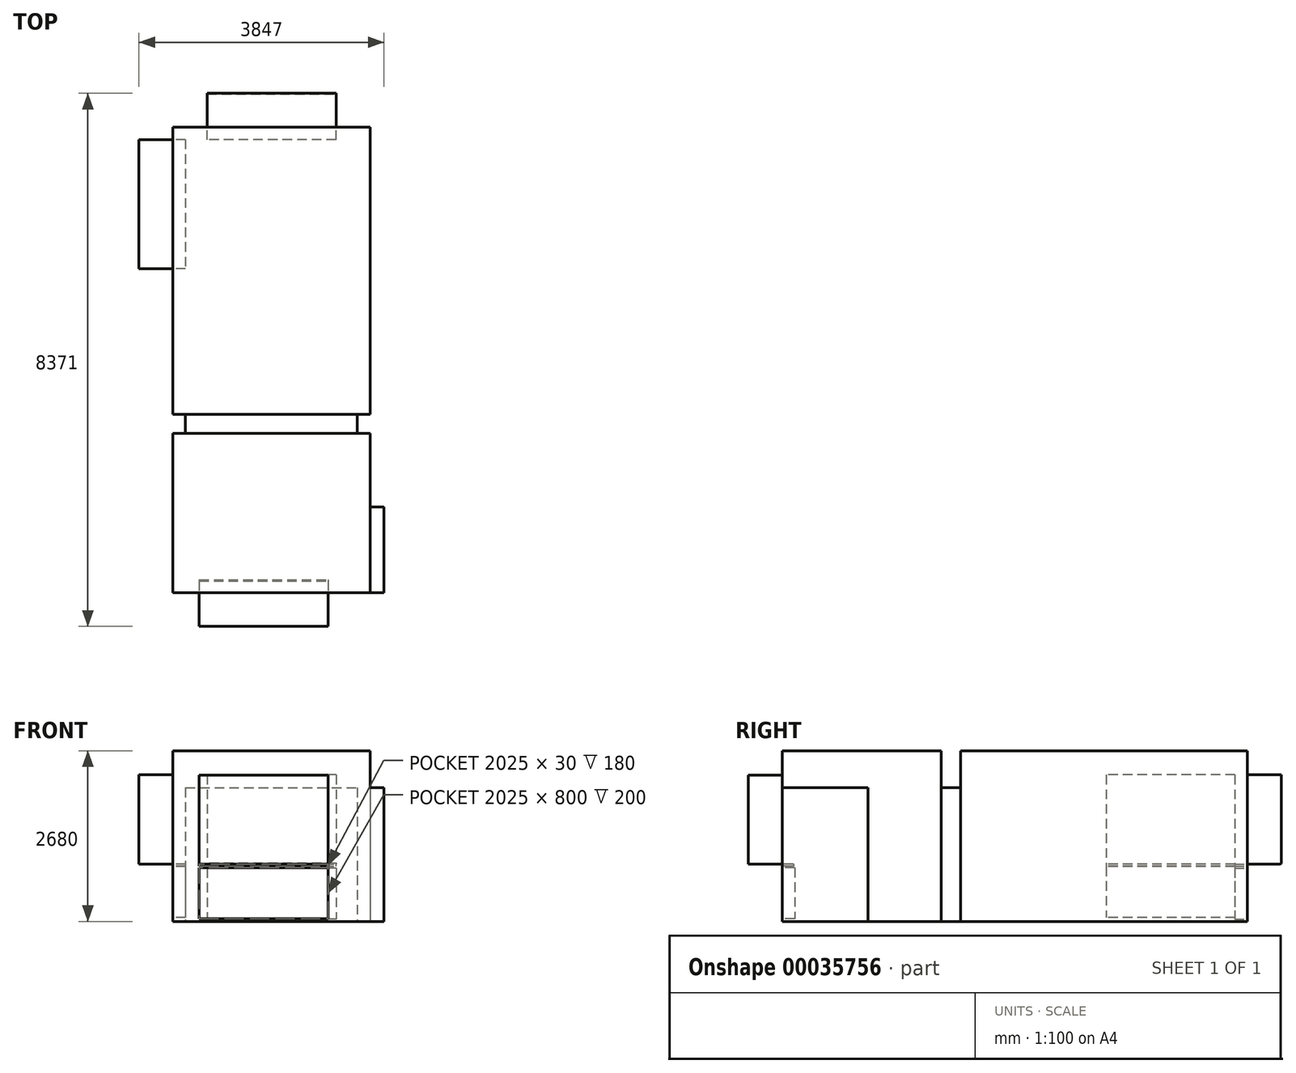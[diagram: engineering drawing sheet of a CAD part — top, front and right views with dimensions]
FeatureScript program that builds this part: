
annotation { "Feature Type Name" : "Feature", "Feature Type Description" : "" }
export const myFeature = defineFeature(function(context is Context, id is Id, definition is map)
    precondition{}
    {
        {
            var Q0;
            Q0=qCreatedBy(makeId("Top.planeOp"),FACE);
            var sketch = newSketch(context, id + "F0", { "sketchPlane" : qUnion([Q0])});
            skLineSegment(sketch, "E0.bottom", {"start": v(-1549.14, 3434.73) * mm, "end": v(1546.86, 3434.73) * mm});
            skLineSegment(sketch, "E0.top", {"start": v(-1549.14, -1072.27) * mm, "end": v(1546.86, -1072.27) * mm});
            skLineSegment(sketch, "E0.left", {"start": v(-1549.14, 3434.73) * mm, "end": v(-1549.14, -1072.27) * mm});
            skLineSegment(sketch, "E0.right", {"start": v(1546.86, 3434.73) * mm, "end": v(1546.86, -1072.27) * mm});
            skSolve(sketch);
        }
        {
            var Q0;
            Q0=makeQuery(id+"F0.imprint","IMPRINT",FACE,{"disambiguationData":[TD([[makeQuery(id+"F0.imprint","IMPRINT",EDGE,{"derivedFrom":sQuery(id+"F0.wireOp",EDGE,"E0.bottom")}),-1.0]])]});
            extrude(context, id + "F1", {"entities" : qUnion([Q0]), "depth" : 2680 * mm});
        }
        {
            var Q0;
            Q0=makeQuery(id+"F1.opExtrude","SWEPT_FACE",FACE,{"disambiguationData":[OSD([sQuery(id+"F0.wireOp",EDGE,"E0.bottom")])]});
            var sketch = newSketch(context, id + "F2", { "sketchPlane" : qUnion([Q0])});
            skLineSegment(sketch, "E1.bottom", {"start": v(-1013.86, 2300) * mm, "end": v(1011.14, 2300) * mm});
            skLineSegment(sketch, "E1.top", {"start": v(-1013.86, 900) * mm, "end": v(1011.14, 900) * mm});
            skLineSegment(sketch, "E1.left", {"start": v(-1013.86, 2300) * mm, "end": v(-1013.86, 900) * mm});
            skLineSegment(sketch, "E1.right", {"start": v(1011.14, 2300) * mm, "end": v(1011.14, 900) * mm});
            skSolve(sketch);
        }
        {
            var Q0;
            Q0=qSketchRegion(id+"F2",true);
            extrude(context, id + "F3", {"entities" : qUnion([Q0]), "operationType" : NewBodyOperationType.ADD, "depth" : 532 * mm});
        }
        {
            var Q0;
            Q0=makeQuery(id+"F1.opExtrude","SWEPT_FACE",FACE,{"disambiguationData":[OSD([sQuery(id+"F0.wireOp",EDGE,"E0.left")])]});
            var sketch = newSketch(context, id + "F4", { "sketchPlane" : qUnion([Q0])});
            skLineSegment(sketch, "E2.bottom", {"start": v(-3238.73, 2300) * mm, "end": v(-1213.73, 2300) * mm});
            skLineSegment(sketch, "E2.top", {"start": v(-3238.73, 900) * mm, "end": v(-1213.73, 900) * mm});
            skLineSegment(sketch, "E2.left", {"start": v(-3238.73, 2300) * mm, "end": v(-3238.73, 900) * mm});
            skLineSegment(sketch, "E2.right", {"start": v(-1213.73, 2300) * mm, "end": v(-1213.73, 900) * mm});
            skSolve(sketch);
        }
        {
            var Q0;
            Q0=makeQuery(id+"F4.imprint","IMPRINT",FACE,{"disambiguationData":[TD([[makeQuery(id+"F4.imprint","IMPRINT",EDGE,{"derivedFrom":sQuery(id+"F4.wireOp",EDGE,"E2.bottom")}),-1.0]])]});
            extrude(context, id + "F5", {"entities" : qUnion([Q0]), "operationType" : NewBodyOperationType.ADD, "depth" : 532 * mm});
        }
        {
            var Q0;
            Q0=makeQuery(id+"F1.opExtrude","SWEPT_FACE",FACE,{"disambiguationData":[OSD([sQuery(id+"F0.wireOp",EDGE,"E0.bottom")])]});
            var sketch = newSketch(context, id + "F6", { "sketchPlane" : qUnion([Q0])});
            skLineSegment(sketch, "E3", {"start": v(1011.14, 900) * mm, "end": v(-1013.86, 900) * mm});
            skLineSegment(sketch, "E4.left", {"start": v(-1013.86, 835) * mm, "end": v(-1013.86, 35) * mm});
            skLineSegment(sketch, "E5.bottom", {"start": v(-1013.86, 835) * mm, "end": v(1011.14, 835) * mm});
            skLineSegment(sketch, "E5.top", {"start": v(-1013.86, 35) * mm, "end": v(1011.14, 35) * mm});
            skLineSegment(sketch, "E5.right", {"start": v(1011.14, 835) * mm, "end": v(1011.14, 35) * mm});
            skSolve(sketch);
        }
        {
            var Q0;
            Q0=makeQuery(id+"F6.imprint","IMPRINT",FACE,{"disambiguationData":[TD([[makeQuery(id+"F6.imprint","IMPRINT",EDGE,{"derivedFrom":sQuery(id+"F6.wireOp",EDGE,"E5.bottom")}),-1.0]])]});
            extrude(context, id + "F7", {"entities" : qUnion([Q0]), "operationType" : NewBodyOperationType.REMOVE, "oppositeDirection" : true, "depth" : 200 * mm});
        }
        {
            var Q0;
            Q0=makeQuery(id+"F1.opExtrude","CAP_FACE",FACE,{"disambiguationData":[OSD([sQuery(id+"F0.wireOp",EDGE,"E0.bottom"),sQuery(id+"F0.wireOp",EDGE,"E0.top"),sQuery(id+"F0.wireOp",EDGE,"E0.left"),sQuery(id+"F0.wireOp",EDGE,"E0.right")])],"isStart":true});
            var sketch = newSketch(context, id + "F8", { "sketchPlane" : qUnion([Q0])});
            skLineSegment(sketch, "E6", {"start": v(-1351.14, 1072.27) * mm, "end": v(-1351.14, 1375.27) * mm});
            skLineSegment(sketch, "E7", {"start": v(-1351.14, 1375.27) * mm, "end": v(1348.86, 1375.27) * mm});
            skLineSegment(sketch, "E8", {"start": v(1348.86, 1375.27) * mm, "end": v(1348.86, 1072.27) * mm});
            skLineSegment(sketch, "E9", {"start": v(1348.86, 1072.27) * mm, "end": v(-1351.14, 1072.27) * mm});
            skSolve(sketch);
        }
        {
            var Q0;
            Q0=makeQuery(id+"F8.imprint","IMPRINT",FACE,{"disambiguationData":[TD([[makeQuery(id+"F8.imprint","IMPRINT",EDGE,{"derivedFrom":sQuery(id+"F8.wireOp",EDGE,"E6")}),-1.0]])]});
            extrude(context, id + "F9", {"entities" : qUnion([Q0]), "operationType" : NewBodyOperationType.ADD, "oppositeDirection" : true, "depth" : 2100 * mm});
        }
        {
            var Q0;
            Q0=makeQuery(id+"F9.boolean.opBoolean","MERGE",FACE,{"derivedFrom":[makeQuery(id+"F1.opExtrude","CAP_FACE",FACE,{"disambiguationData":[OSD([sQuery(id+"F0.wireOp",EDGE,"E0.bottom"),sQuery(id+"F0.wireOp",EDGE,"E0.top"),sQuery(id+"F0.wireOp",EDGE,"E0.left"),sQuery(id+"F0.wireOp",EDGE,"E0.right")])],"isStart":true}),makeQuery(id+"F9.opExtrude","CAP_FACE",FACE,{"disambiguationData":[OSD([sQuery(id+"F8.wireOp",EDGE,"E6"),sQuery(id+"F8.wireOp",EDGE,"E7"),sQuery(id+"F8.wireOp",EDGE,"E8"),sQuery(id+"F8.wireOp",EDGE,"E9")])],"isStart":true})]});
            var sketch = newSketch(context, id + "F10", { "sketchPlane" : qUnion([Q0])});
            skLineSegment(sketch, "E10.bottom", {"start": v(-1549.14, 1375.27) * mm, "end": v(1546.86, 1375.27) * mm});
            skLineSegment(sketch, "E10.top", {"start": v(-1549.14, 3872.27) * mm, "end": v(1546.86, 3872.27) * mm});
            skLineSegment(sketch, "E10.left", {"start": v(-1549.14, 1375.27) * mm, "end": v(-1549.14, 3872.27) * mm});
            skLineSegment(sketch, "E10.right", {"start": v(1546.86, 1375.27) * mm, "end": v(1546.86, 3872.27) * mm});
            skLineSegment(sketch, "E11", {"start": v(-1549.14, 1375.27) * mm, "end": v(-1351.14, 1375.27) * mm});
            skSolve(sketch);
        }
        {
            var Q0;
            Q0=qSketchRegion(id+"F10",true);
            extrude(context, id + "F11", {"entities" : qUnion([Q0]), "operationType" : NewBodyOperationType.ADD, "oppositeDirection" : true, "depth" : 2680 * mm});
        }
        {
            var Q0;
            Q0=makeQuery(id+"F11.boolean.opBoolean","MERGE",FACE,{"derivedFrom":[makeQuery(id+"F9.boolean.opBoolean","MERGE",FACE,{"derivedFrom":[makeQuery(id+"F1.opExtrude","CAP_FACE",FACE,{"disambiguationData":[OSD([sQuery(id+"F0.wireOp",EDGE,"E0.bottom"),sQuery(id+"F0.wireOp",EDGE,"E0.top"),sQuery(id+"F0.wireOp",EDGE,"E0.left"),sQuery(id+"F0.wireOp",EDGE,"E0.right")])],"isStart":true}),makeQuery(id+"F9.opExtrude","CAP_FACE",FACE,{"disambiguationData":[OSD([sQuery(id+"F8.wireOp",EDGE,"E6"),sQuery(id+"F8.wireOp",EDGE,"E7"),sQuery(id+"F8.wireOp",EDGE,"E8"),sQuery(id+"F8.wireOp",EDGE,"E9")])],"isStart":true})]}),makeQuery(id+"F11.opExtrude","CAP_FACE",FACE,{"disambiguationData":[OSD([sQuery(id+"F10.wireOp",EDGE,"E10.bottom"),sQuery(id+"F10.wireOp",EDGE,"E10.top"),sQuery(id+"F10.wireOp",EDGE,"E10.left"),sQuery(id+"F10.wireOp",EDGE,"E10.right"),sQuery(id+"F10.wireOp",EDGE,"E11")])],"isStart":true})]});
            var sketch = newSketch(context, id + "F12", { "sketchPlane" : qUnion([Q0])});
            skLineSegment(sketch, "E12.bottom", {"start": v(1546.86, 3872.27) * mm, "end": v(1765.86, 3872.27) * mm});
            skLineSegment(sketch, "E12.top", {"start": v(1546.86, 2526.27) * mm, "end": v(1765.86, 2526.27) * mm});
            skLineSegment(sketch, "E12.left", {"start": v(1546.86, 3872.27) * mm, "end": v(1546.86, 2526.27) * mm});
            skLineSegment(sketch, "E12.right", {"start": v(1765.86, 3872.27) * mm, "end": v(1765.86, 2526.27) * mm});
            skSolve(sketch);
        }
        {
            var Q0;
            Q0=makeQuery(id+"F12.imprint","IMPRINT",FACE,{"disambiguationData":[TD([[makeQuery(id+"F12.imprint","IMPRINT",EDGE,{"derivedFrom":sQuery(id+"F12.wireOp",EDGE,"E12.bottom")}),-1.0]])]});
            extrude(context, id + "F13", {"entities" : qUnion([Q0]), "operationType" : NewBodyOperationType.ADD, "oppositeDirection" : true, "depth" : 2100 * mm});
        }
        {
            var Q0;
            Q0=makeQuery(id+"F13.boolean.opBoolean","MERGE",FACE,{"derivedFrom":[makeQuery(id+"F11.opExtrude","SWEPT_FACE",FACE,{"disambiguationData":[OSD([sQuery(id+"F10.wireOp",EDGE,"E10.top")])]}),makeQuery(id+"F13.opExtrude","SWEPT_FACE",FACE,{"disambiguationData":[OSD([sQuery(id+"F12.wireOp",EDGE,"E12.bottom")])]})]});
            var sketch = newSketch(context, id + "F14", { "sketchPlane" : qUnion([Q0])});
            skLineSegment(sketch, "E13.bottom", {"start": v(-1134.15, 2296.53) * mm, "end": v(890.85, 2296.53) * mm});
            skLineSegment(sketch, "E13.top", {"start": v(-1134.15, 896.53) * mm, "end": v(890.85, 896.53) * mm});
            skLineSegment(sketch, "E13.left", {"start": v(-1134.15, 2296.53) * mm, "end": v(-1134.15, 896.53) * mm});
            skLineSegment(sketch, "E13.right", {"start": v(890.85, 2296.53) * mm, "end": v(890.85, 896.53) * mm});
            skSolve(sketch);
        }
        {
            var Q0;
            Q0=makeQuery(id+"F14.imprint","IMPRINT",FACE,{"disambiguationData":[TD([[makeQuery(id+"F14.imprint","IMPRINT",EDGE,{"derivedFrom":sQuery(id+"F14.wireOp",EDGE,"E13.bottom")}),-1.0]])]});
            extrude(context, id + "F15", {"entities" : qUnion([Q0]), "operationType" : NewBodyOperationType.ADD, "depth" : 532 * mm});
        }
        {
            var Q0;
            Q0=makeQuery(id+"F12.imprint","IMPRINT",FACE,{"disambiguationData":[TD([[makeQuery(id+"F12.imprint","IMPRINT",EDGE,{"derivedFrom":sQuery(id+"F12.wireOp",EDGE,"E12.bottom")}),-1.0]])]});
            var sketch = newSketch(context, id + "F16", { "sketchPlane" : qUnion([Q0])});
            skLineSegment(sketch, "E14", {"start": v(1765.86, 3872.27) * mm, "end": v(2057.86, 3872.27) * mm});
            skLineSegment(sketch, "E15", {"start": v(2057.86, 3872.27) * mm, "end": v(2057.86, 5091.27) * mm});
            skLineSegment(sketch, "E16", {"start": v(1765.86, 3872.27) * mm, "end": v(1765.86, 2474.27) * mm});
            skLineSegment(sketch, "E17", {"start": v(1765.86, 2474.27) * mm, "end": v(2915.86, 2474.27) * mm});
            skLineSegment(sketch, "E18", {"start": v(2915.86, 2474.27) * mm, "end": v(2915.86, 2739.27) * mm});
            skLineSegment(sketch, "E19", {"start": v(2915.86, 2739.27) * mm, "end": v(5096.86, 2739.27) * mm});
            skLineSegment(sketch, "E20", {"start": v(5096.86, 2739.27) * mm, "end": v(5096.86, 5091.27) * mm});
            skLineSegment(sketch, "E21", {"start": v(2057.86, 5091.27) * mm, "end": v(5096.86, 5091.27) * mm});
            skSolve(sketch);
        }
        {
            var Q0;
            Q0=makeQuery(id+"F3.opExtrude","CAP_EDGE",EDGE,{"disambiguationData":[OSD([sQuery(id+"F2.wireOp",EDGE,"E1.top")])],"isStart":false});
            chamfer(context, id + "F17", {"entities" : qUnion([Q0]), "width" : 10 * mm, "tangentPropagation" : true});
        }
        {
            var Q0;
            Q0=makeQuery(id+"F1.opExtrude","SWEPT_FACE",FACE,{"disambiguationData":[OSD([sQuery(id+"F0.wireOp",EDGE,"E0.left")])]});
            var sketch = newSketch(context, id + "F18", { "sketchPlane" : qUnion([Q0])});
            skLineSegment(sketch, "E22.left", {"start": v(-3238.73, 860) * mm, "end": v(-3238.73, 60) * mm});
            skLineSegment(sketch, "E23.bottom", {"start": v(-3238.73, 860) * mm, "end": v(-1213.73, 860) * mm});
            skLineSegment(sketch, "E23.top", {"start": v(-3238.73, 60) * mm, "end": v(-1213.73, 60) * mm});
            skLineSegment(sketch, "E23.right", {"start": v(-1213.73, 860) * mm, "end": v(-1213.73, 60) * mm});
            skSolve(sketch);
        }
        {
            var Q0;
            Q0=makeQuery(id+"F1.opExtrude","SWEPT_FACE",FACE,{"disambiguationData":[OSD([sQuery(id+"F0.wireOp",EDGE,"E0.bottom")])]});
            var sketch = newSketch(context, id + "F19", { "sketchPlane" : qUnion([Q0])});
            skLineSegment(sketch, "E24", {"start": v(-1013.86, 900) * mm, "end": v(1011.14, 900) * mm});
            skLineSegment(sketch, "E25", {"start": v(1011.14, 900) * mm, "end": v(1011.14, 870) * mm});
            skLineSegment(sketch, "E26", {"start": v(1011.14, 870) * mm, "end": v(-1013.86, 870) * mm});
            skLineSegment(sketch, "E27", {"start": v(-1013.86, 870) * mm, "end": v(-1013.86, 900) * mm});
            skSolve(sketch);
        }
        {
            var Q0;
            Q0=makeQuery(id+"F19.imprint","IMPRINT",FACE,{"disambiguationData":[TD([[makeQuery(id+"F19.imprint","IMPRINT",EDGE,{"derivedFrom":sQuery(id+"F19.wireOp",EDGE,"E24")}),-1.0]])]});
            extrude(context, id + "F20", {"entities" : qUnion([Q0]), "operationType" : NewBodyOperationType.REMOVE, "oppositeDirection" : true, "depth" : 200 * mm});
        }
        {
            var Q0;
            Q0=makeQuery(id+"FVY1y7tDIZpeI0f_3.boolean.opBoolean","MERGE",FACE,{"derivedFrom":[makeQuery(id+"F13.boolean.opBoolean","MERGE",FACE,{"derivedFrom":[makeQuery(id+"F11.opExtrude","SWEPT_FACE",FACE,{"disambiguationData":[OSD([sQuery(id+"F10.wireOp",EDGE,"E10.top")])]}),makeQuery(id+"F13.opExtrude","SWEPT_FACE",FACE,{"disambiguationData":[OSD([sQuery(id+"F12.wireOp",EDGE,"E12.bottom")])]})]}),makeQuery(id+"FVY1y7tDIZpeI0f_3.opExtrude","SWEPT_FACE",FACE,{"disambiguationData":[OSD([sQuery(id+"F16.wireOp",EDGE,"E14")])]})]});
            var sketch = newSketch(context, id + "F21", { "sketchPlane" : qUnion([Q0])});
            skLineSegment(sketch, "E28.bottom", {"start": v(-1134.15, 896.53) * mm, "end": v(890.85, 896.53) * mm});
            skLineSegment(sketch, "E28.top", {"start": v(-1134.15, 866.53) * mm, "end": v(890.85, 866.53) * mm});
            skLineSegment(sketch, "E28.left", {"start": v(-1134.15, 896.53) * mm, "end": v(-1134.15, 866.53) * mm});
            skLineSegment(sketch, "E28.right", {"start": v(890.85, 896.53) * mm, "end": v(890.85, 866.53) * mm});
            skSolve(sketch);
        }
        {
            var Q0;
            Q0=makeQuery(id+"F21.imprint","IMPRINT",FACE,{"disambiguationData":[TD([[makeQuery(id+"F21.imprint","IMPRINT",EDGE,{"derivedFrom":sQuery(id+"F21.wireOp",EDGE,"E28.bottom")}),-1.0]])]});
            extrude(context, id + "F22", {"entities" : qUnion([Q0]), "operationType" : NewBodyOperationType.REMOVE, "oppositeDirection" : true, "depth" : 180 * mm});
        }
        {
            var Q0;
            Q0=makeQuery(id+"F18.imprint","IMPRINT",FACE,{"disambiguationData":[TD([[makeQuery(id+"F18.imprint","IMPRINT",EDGE,{"derivedFrom":sQuery(id+"F18.wireOp",EDGE,"E23.bottom")}),-1.0]])]});
            extrude(context, id + "F23", {"entities" : qUnion([Q0]), "operationType" : NewBodyOperationType.REMOVE, "oppositeDirection" : true, "depth" : 200 * mm});
        }
        {
            var Q0;
            {var subQ0=sQuery(id+"F0.wireOp",EDGE,"E0.left");var subQ1=sQuery(id+"F0.wireOp",EDGE,"E0.bottom");Q0=makeQuery(id+"F23.boolean.opBoolean","SPLIT",FACE,{"disambiguationData":[TD([makeQuery(id+"F1.opExtrude","SWEPT_FACE",FACE,{"disambiguationData":[OSD([subQ1])]})])],"derivedFrom":makeQuery(id+"F1.opExtrude","SWEPT_FACE",FACE,{"disambiguationData":[OSD([subQ0])]})});}
            var sketch = newSketch(context, id + "F24", { "sketchPlane" : qUnion([Q0])});
            skLineSegment(sketch, "E29.bottom", {"start": v(-3238.73, 900) * mm, "end": v(-1213.73, 900) * mm});
            skLineSegment(sketch, "E29.top", {"start": v(-3238.73, 870) * mm, "end": v(-1213.73, 870) * mm});
            skLineSegment(sketch, "E29.left", {"start": v(-3238.73, 900) * mm, "end": v(-3238.73, 870) * mm});
            skLineSegment(sketch, "E29.right", {"start": v(-1213.73, 900) * mm, "end": v(-1213.73, 870) * mm});
            skSolve(sketch);
        }
        {
            var Q0;
            Q0=makeQuery(id+"F24.imprint","IMPRINT",FACE,{"disambiguationData":[TD([[makeQuery(id+"F24.imprint","IMPRINT",EDGE,{"derivedFrom":sQuery(id+"F24.wireOp",EDGE,"E29.bottom")}),-1.0]])]});
            extrude(context, id + "F25", {"entities" : qUnion([Q0]), "operationType" : NewBodyOperationType.REMOVE, "oppositeDirection" : true, "depth" : 200 * mm});
        }
        {
            var Q0;
            Q0=makeQuery(id+"FVY1y7tDIZpeI0f_3.boolean.opBoolean","MERGE",FACE,{"derivedFrom":[makeQuery(id+"F13.boolean.opBoolean","MERGE",FACE,{"derivedFrom":[makeQuery(id+"F11.opExtrude","SWEPT_FACE",FACE,{"disambiguationData":[OSD([sQuery(id+"F10.wireOp",EDGE,"E10.top")])]}),makeQuery(id+"F13.opExtrude","SWEPT_FACE",FACE,{"disambiguationData":[OSD([sQuery(id+"F12.wireOp",EDGE,"E12.bottom")])]})]}),makeQuery(id+"FVY1y7tDIZpeI0f_3.opExtrude","SWEPT_FACE",FACE,{"disambiguationData":[OSD([sQuery(id+"F16.wireOp",EDGE,"E14")])]})]});
            var sketch = newSketch(context, id + "F26", { "sketchPlane" : qUnion([Q0])});
            skLineSegment(sketch, "E30.left", {"start": v(-1134.15, 841.53) * mm, "end": v(-1134.15, 41.53) * mm});
            skLineSegment(sketch, "E31.bottom", {"start": v(-1134.15, 841.53) * mm, "end": v(890.85, 841.53) * mm});
            skLineSegment(sketch, "E31.top", {"start": v(-1134.15, 41.53) * mm, "end": v(890.85, 41.53) * mm});
            skLineSegment(sketch, "E31.right", {"start": v(890.85, 841.53) * mm, "end": v(890.85, 41.53) * mm});
            skSolve(sketch);
        }
        {
            var Q0;
            Q0=qSketchRegion(id+"F26",true);
            extrude(context, id + "F27", {"entities" : qUnion([Q0]), "operationType" : NewBodyOperationType.REMOVE, "oppositeDirection" : true, "depth" : 200 * mm});
        }
    });
